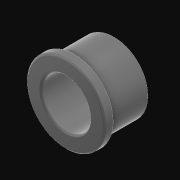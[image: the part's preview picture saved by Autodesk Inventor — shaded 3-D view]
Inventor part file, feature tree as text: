
AUTODESK INVENTOR PART (.ipt)
format: ipt  version: 2021 (Build 250183000, 183)  size: 194,560 bytes
history: native  units: in
note: dims shown in document units (in); Inventor stores cm internally (conversion verified against a paired STEP export)
features: fillet x1
ambient origin geometry x8: Origin, YZ Plane, XZ Plane, XY Plane, X Axis, Y Axis, Z Axis, Center Point
bodies: Solid1 (feature_tree)
feature tree (1):
  fillet  "Fillet1"  [1 undecoded]
note: 1 required parameter value undecoded (feature->parameter linkage not recoverable at this tier; creation-order binding heuristic only, values carry confidence <= 0.55)
